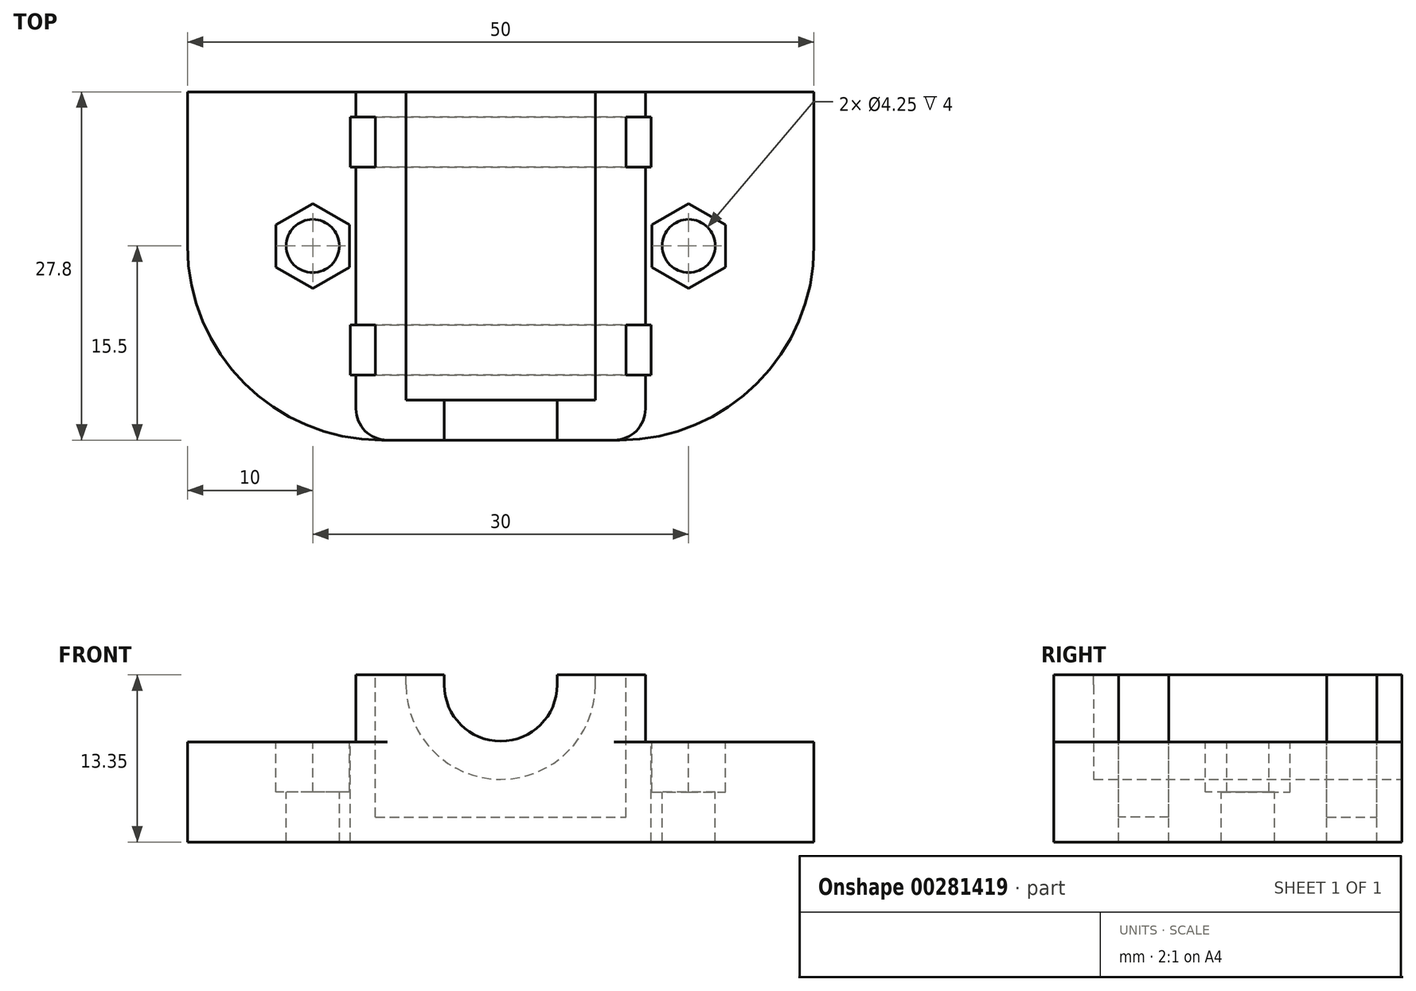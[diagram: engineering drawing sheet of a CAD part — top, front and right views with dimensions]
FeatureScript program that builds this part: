
annotation { "Feature Type Name" : "Feature", "Feature Type Description" : "" }
export const myFeature = defineFeature(function(context is Context, id is Id, definition is map)
    precondition{}
    {
        {
            var Q0;
            Q0=qCreatedBy(makeId("Front.planeOp"),FACE);
            var sketch = newSketch(context, id + "F0", { "sketchPlane" : qUnion([Q0])});
            skLineSegment(sketch, "E0.bottom", {"start": v(25, -4) * mm, "end": v(-25, -4) * mm});
            skLineSegment(sketch, "E0.top", {"start": v(25, 4) * mm, "end": v(11.55, 4) * mm});
            skLineSegment(sketch, "E0.left", {"start": v(25, -4) * mm, "end": v(25, 4) * mm});
            skLineSegment(sketch, "E0.right", {"start": v(-25, -4) * mm, "end": v(-25, 4) * mm});
            skPoint(sketch, "E0.middle", {"position": v(0, 0) * mm});
            skArc(sketch, "E1", {"start": v(7.55, 8.55) * mm, "mid": v(0, 1) * mm, "end": v(-7.55, 8.55) * mm});
            skLineSegment(sketch, "E2", {"start": v(-7.55, 9.35) * mm, "end": v(-11.55, 9.35) * mm});
            skLineSegment(sketch, "E3", {"start": v(-11.55, 9.35) * mm, "end": v(-11.55, 4) * mm});
            skLineSegment(sketch, "E4", {"start": v(-7.55, 8.55) * mm, "end": v(-7.55, 9.35) * mm});
            skLineSegment(sketch, "E5.MirrorCS", {"start": v(7.55, 8.55) * mm, "end": v(7.55, 9.35) * mm});
            skLineSegment(sketch, "E6.MirrorCS", {"start": v(7.55, 9.35) * mm, "end": v(11.55, 9.35) * mm});
            skLineSegment(sketch, "E7.MirrorCS", {"start": v(11.55, 9.35) * mm, "end": v(11.55, 4) * mm});
            skLineSegment(sketch, "E8.trimOffspring", {"start": v(-11.55, 4) * mm, "end": v(-25, 4) * mm});
            skSolve(sketch);
        }
        {
            var Q0;
            Q0=qSketchRegion(id+"F0",true);
            extrude(context, id + "F1", {"entities" : qUnion([Q0]), "endBound" : BoundingType.SYMMETRIC, "depth" : 24.6 * mm});
        }
        {
            var Q0;
            Q0=makeQuery(id+"F1.opExtrude","CAP_FACE",FACE,{"disambiguationData":[OSD([sQuery(id+"F0.wireOp",EDGE,"E0.bottom"),sQuery(id+"F0.wireOp",EDGE,"E0.top"),sQuery(id+"F0.wireOp",EDGE,"E0.left"),sQuery(id+"F0.wireOp",EDGE,"E0.right"),sQuery(id+"F0.wireOp",EDGE,"E1"),sQuery(id+"F0.wireOp",EDGE,"E2"),sQuery(id+"F0.wireOp",EDGE,"E3"),sQuery(id+"F0.wireOp",EDGE,"E4"),sQuery(id+"F0.wireOp",EDGE,"E5.MirrorCS"),sQuery(id+"F0.wireOp",EDGE,"E6.MirrorCS"),sQuery(id+"F0.wireOp",EDGE,"E7.MirrorCS"),sQuery(id+"F0.wireOp",EDGE,"E8.trimOffspring")])],"isStart":false});
            var sketch = newSketch(context, id + "F2", { "sketchPlane" : qUnion([Q0])});
            skArc(sketch, "E9", {"start": v(4.5, 8.55) * mm, "mid": v(0, 4.05) * mm, "end": v(-4.5, 8.55) * mm});
            skLineSegment(sketch, "E10", {"start": v(4.5, 8.55) * mm, "end": v(4.5, 9.35) * mm});
            skLineSegment(sketch, "E11", {"start": v(4.5, 9.35) * mm, "end": v(11.55, 9.35) * mm});
            skLineSegment(sketch, "E12", {"start": v(11.55, 9.35) * mm, "end": v(11.55, 4) * mm});
            skLineSegment(sketch, "E13", {"start": v(11.55, 4) * mm, "end": v(25, 4) * mm});
            skLineSegment(sketch, "E14", {"start": v(25, 4) * mm, "end": v(25, -4) * mm});
            skLineSegment(sketch, "E15", {"start": v(25, -4) * mm, "end": v(-25, -4) * mm});
            skLineSegment(sketch, "E16", {"start": v(-25, -4) * mm, "end": v(-25, 4) * mm});
            skLineSegment(sketch, "E17", {"start": v(-25, 4) * mm, "end": v(-11.55, 4) * mm});
            skLineSegment(sketch, "E18", {"start": v(-11.55, 4) * mm, "end": v(-11.55, 9.35) * mm});
            skLineSegment(sketch, "E19", {"start": v(-11.55, 9.35) * mm, "end": v(-4.5, 9.35) * mm});
            skLineSegment(sketch, "E20", {"start": v(-4.5, 9.35) * mm, "end": v(-4.5, 8.55) * mm});
            skSolve(sketch);
        }
        {
            var Q0;
            Q0=qSketchRegion(id+"F2",true);
            extrude(context, id + "F3", {"entities" : qUnion([Q0]), "operationType" : NewBodyOperationType.ADD, "depth" : 3.2 * mm});
        }
        {
            var Q0;
            {var subQ0=sQuery(id+"F2.wireOp",EDGE,"E17");Q0=makeQuery(id+"FOkd2pxTrmwczwa_1.1.F3.boolean.opBoolean","MERGE",FACE,{"derivedFrom":[makeQuery(id+"F3.boolean.opBoolean","MERGE",FACE,{"derivedFrom":[makeQuery(id+"F1.opExtrude","SWEPT_FACE",FACE,{"disambiguationData":[OSD([sQuery(id+"F0.wireOp",EDGE,"E8.trimOffspring")])]}),makeQuery(id+"F3.opExtrude","SWEPT_FACE",FACE,{"disambiguationData":[OSD([subQ0])]})]}),makeQuery(id+"FOkd2pxTrmwczwa_1.1.F3.opExtrude","SWEPT_FACE",FACE,{"disambiguationData":[OSD([subQ0])]})]});}
            var sketch = newSketch(context, id + "F4", { "sketchPlane" : qUnion([Q0])});
            skCircle(sketch, "E21", {"center": v(-15, 0) * mm, "radius": 2.12 * mm});
            skCircle(sketch, "E22", {"center": v(15, 0) * mm, "radius": 2.12 * mm});
            skLineSegment(sketch, "E23.bottom", {"start": v(10, 10.3) * mm, "end": v(12, 10.3) * mm});
            skLineSegment(sketch, "E23.top", {"start": v(10, 6.3) * mm, "end": v(12, 6.3) * mm});
            skLineSegment(sketch, "E23.left", {"start": v(10, 10.3) * mm, "end": v(10, 6.3) * mm});
            skLineSegment(sketch, "E23.right", {"start": v(12, 10.3) * mm, "end": v(12, 6.3) * mm});
            skLineSegment(sketch, "E24.MirrorCS", {"start": v(10, -10.3) * mm, "end": v(10, -6.3) * mm});
            skLineSegment(sketch, "E25.MirrorCS", {"start": v(12, -10.3) * mm, "end": v(12, -6.3) * mm});
            skLineSegment(sketch, "E26.MirrorCS", {"start": v(10, -10.3) * mm, "end": v(12, -10.3) * mm});
            skLineSegment(sketch, "E27.MirrorCS", {"start": v(10, -6.3) * mm, "end": v(12, -6.3) * mm});
            skLineSegment(sketch, "E28.MirrorCS", {"start": v(-10, -6.3) * mm, "end": v(-12, -6.3) * mm});
            skLineSegment(sketch, "E29.MirrorCS", {"start": v(-10, 6.3) * mm, "end": v(-12, 6.3) * mm});
            skLineSegment(sketch, "E30.MirrorCS", {"start": v(-10, -10.3) * mm, "end": v(-12, -10.3) * mm});
            skLineSegment(sketch, "E31.MirrorCS", {"start": v(-10, 10.3) * mm, "end": v(-12, 10.3) * mm});
            skLineSegment(sketch, "E32.MirrorCS", {"start": v(-12, 10.3) * mm, "end": v(-12, 6.3) * mm});
            skLineSegment(sketch, "E33.MirrorCS", {"start": v(-10, -10.3) * mm, "end": v(-10, -6.3) * mm});
            skLineSegment(sketch, "E34.MirrorCS", {"start": v(-12, -10.3) * mm, "end": v(-12, -6.3) * mm});
            skLineSegment(sketch, "E35.MirrorCS", {"start": v(-10, 10.3) * mm, "end": v(-10, 6.3) * mm});
            skSolve(sketch);
        }
        {
            var Q0;
            Q0=qSketchRegion(id+"F4",true);
            extrude(context, id + "F5", {"entities" : qUnion([Q0]), "operationType" : NewBodyOperationType.REMOVE, "endBound" : BoundingType.THROUGH_ALL, "oppositeDirection" : true, "depth" : 25 * mm});
        }
        {
            var Q0;
            {var subQ0=sQuery(id+"F2.wireOp",EDGE,"E15");Q0=makeQuery(id+"FOkd2pxTrmwczwa_1.1.F3.boolean.opBoolean","MERGE",FACE,{"derivedFrom":[makeQuery(id+"F3.boolean.opBoolean","MERGE",FACE,{"derivedFrom":[makeQuery(id+"F1.opExtrude","SWEPT_FACE",FACE,{"disambiguationData":[OSD([sQuery(id+"F0.wireOp",EDGE,"E0.bottom")])]}),makeQuery(id+"F3.opExtrude","SWEPT_FACE",FACE,{"disambiguationData":[OSD([subQ0])]})]}),makeQuery(id+"FOkd2pxTrmwczwa_1.1.F3.opExtrude","SWEPT_FACE",FACE,{"disambiguationData":[OSD([subQ0])]})]});}
            var sketch = newSketch(context, id + "F6", { "sketchPlane" : qUnion([Q0])});
            skLineSegment(sketch, "E36.bottom", {"start": v(-10, 6.3) * mm, "end": v(10, 6.3) * mm});
            skLineSegment(sketch, "E36.top", {"start": v(-10, 10.3) * mm, "end": v(10, 10.3) * mm});
            skLineSegment(sketch, "E36.left", {"start": v(-10, 6.3) * mm, "end": v(-10, 10.3) * mm});
            skLineSegment(sketch, "E36.right", {"start": v(10, 6.3) * mm, "end": v(10, 10.3) * mm});
            skLineSegment(sketch, "E37.bottom", {"start": v(-10, -6.3) * mm, "end": v(10, -6.3) * mm});
            skLineSegment(sketch, "E37.top", {"start": v(-10, -10.3) * mm, "end": v(10, -10.3) * mm});
            skLineSegment(sketch, "E37.left", {"start": v(-10, -6.3) * mm, "end": v(-10, -10.3) * mm});
            skLineSegment(sketch, "E37.right", {"start": v(10, -6.3) * mm, "end": v(10, -10.3) * mm});
            skSolve(sketch);
        }
        {
            var Q0;
            Q0=qSketchRegion(id+"F6",true);
            extrude(context, id + "F7", {"entities" : qUnion([Q0]), "operationType" : NewBodyOperationType.REMOVE, "oppositeDirection" : true, "depth" : 2 * mm});
        }
        {
            var Q0;
            Q0=makeQuery(id+"FOkd2pxTrmwczwa_1.1.F3.opExtrude","CAP_EDGE",EDGE,{"disambiguationData":[OSD([sQuery(id+"F2.wireOp",EDGE,"E16")])],"isStart":false});
            var Q1;
            Q1=makeQuery(id+"F3.opExtrude","CAP_EDGE",EDGE,{"disambiguationData":[OSD([sQuery(id+"F2.wireOp",EDGE,"E16")])],"isStart":false});
            var Q2;
            Q2=makeQuery(id+"FOkd2pxTrmwczwa_1.1.F3.opExtrude","CAP_EDGE",EDGE,{"disambiguationData":[OSD([sQuery(id+"F2.wireOp",EDGE,"E14")])],"isStart":false});
            var Q3;
            Q3=makeQuery(id+"F3.opExtrude","CAP_EDGE",EDGE,{"disambiguationData":[OSD([sQuery(id+"F2.wireOp",EDGE,"E14")])],"isStart":false});
            fillet(context, id + "F8", {"entities" : qUnion([Q0, Q1, Q2, Q3]), "radius" : 15.5 * mm, "tangentPropagation" : true, "allowEdgeOverflow" : false});
        }
        {
            var Q0;
            {var subQ0=sQuery(id+"F2.wireOp",EDGE,"E13");Q0=makeQuery(id+"FOkd2pxTrmwczwa_1.1.F3.boolean.opBoolean","MERGE",FACE,{"derivedFrom":[makeQuery(id+"F3.boolean.opBoolean","MERGE",FACE,{"derivedFrom":[makeQuery(id+"F1.opExtrude","SWEPT_FACE",FACE,{"disambiguationData":[OSD([sQuery(id+"F0.wireOp",EDGE,"E0.top")])]}),makeQuery(id+"F3.opExtrude","SWEPT_FACE",FACE,{"disambiguationData":[OSD([subQ0])]})]}),makeQuery(id+"FOkd2pxTrmwczwa_1.1.F3.opExtrude","SWEPT_FACE",FACE,{"disambiguationData":[OSD([subQ0])]})]});}
            var sketch = newSketch(context, id + "F9", { "sketchPlane" : qUnion([Q0])});
            skCircle(sketch, "E38.cCircle", {"center": v(15, 0) * mm, "radius": 2.93 * mm, "construction": true});
            skLineSegment(sketch, "E38.0", {"start": v(17.93, 1.69) * mm, "end": v(17.93, -1.69) * mm});
            skLineSegment(sketch, "E38.1", {"start": v(17.93, -1.69) * mm, "end": v(15, -3.38) * mm});
            skLineSegment(sketch, "E38.2", {"start": v(15, -3.38) * mm, "end": v(12.08, -1.69) * mm});
            skLineSegment(sketch, "E38.3", {"start": v(12.08, -1.69) * mm, "end": v(12.08, 1.69) * mm});
            skLineSegment(sketch, "E38.4", {"start": v(12.08, 1.69) * mm, "end": v(15, 3.38) * mm});
            skLineSegment(sketch, "E38.5", {"start": v(15, 3.38) * mm, "end": v(17.93, 1.69) * mm});
            skPoint(sketch, "E38.0.midPoint", {"position": v(17.93, 0) * mm});
            skLineSegment(sketch, "E39.MirrorCS", {"start": v(-12.08, -1.69) * mm, "end": v(-12.08, 1.69) * mm});
            skLineSegment(sketch, "E40.MirrorCS", {"start": v(-15, -3.38) * mm, "end": v(-12.08, -1.69) * mm});
            skLineSegment(sketch, "E41.MirrorCS", {"start": v(-17.93, 1.69) * mm, "end": v(-17.93, -1.69) * mm});
            skLineSegment(sketch, "E42.MirrorCS", {"start": v(-15, 3.38) * mm, "end": v(-17.93, 1.69) * mm});
            skLineSegment(sketch, "E43.MirrorCS", {"start": v(-12.08, 1.69) * mm, "end": v(-15, 3.38) * mm});
            skLineSegment(sketch, "E44.MirrorCS", {"start": v(-17.93, -1.69) * mm, "end": v(-15, -3.38) * mm});
            skCircle(sketch, "E45.MirrorC", {"center": v(-15, 0) * mm, "radius": 2.93 * mm, "construction": true});
            skPoint(sketch, "E46.MirrorP", {"position": v(-17.93, 0) * mm});
            skSolve(sketch);
        }
        {
            var Q0;
            Q0=qSketchRegion(id+"F9",true);
            extrude(context, id + "F10", {"entities" : qUnion([Q0]), "operationType" : NewBodyOperationType.REMOVE, "oppositeDirection" : true, "depth" : 4 * mm});
        }
        {
            var Q0;
            {var subQ0=sQuery(id+"F2.wireOp",EDGE,"E18");Q0=makeQuery(id+"F8.opFillet","BLEND_EDGE",EDGE,{"blendedFrom":[makeQuery(id+"FOkd2pxTrmwczwa_1.1.F3.opExtrude","CAP_EDGE",EDGE,{"disambiguationData":[OSD([sQuery(id+"F2.wireOp",EDGE,"E16")])],"isStart":false}),makeQuery(id+"FOkd2pxTrmwczwa_1.1.F3.boolean.opBoolean","MERGE",FACE,{"derivedFrom":[makeQuery(id+"F3.boolean.opBoolean","MERGE",FACE,{"derivedFrom":[makeQuery(id+"F1.opExtrude","SWEPT_FACE",FACE,{"disambiguationData":[OSD([sQuery(id+"F0.wireOp",EDGE,"E3")])]}),makeQuery(id+"F3.opExtrude","SWEPT_FACE",FACE,{"disambiguationData":[OSD([subQ0])]})]}),makeQuery(id+"FOkd2pxTrmwczwa_1.1.F3.opExtrude","SWEPT_FACE",FACE,{"disambiguationData":[OSD([subQ0])]})]})],"blendedInto":[makeQuery(id+"FOkd2pxTrmwczwa_1.1.F3.boolean.opBoolean","MERGE",FACE,{"derivedFrom":[makeQuery(id+"F3.boolean.opBoolean","MERGE",FACE,{"derivedFrom":[makeQuery(id+"F1.opExtrude","SWEPT_FACE",FACE,{"disambiguationData":[OSD([sQuery(id+"F0.wireOp",EDGE,"E3")])]}),makeQuery(id+"F3.opExtrude","SWEPT_FACE",FACE,{"disambiguationData":[OSD([subQ0])]})]}),makeQuery(id+"FOkd2pxTrmwczwa_1.1.F3.opExtrude","SWEPT_FACE",FACE,{"disambiguationData":[OSD([subQ0])]})]})]});}
            var Q1;
            {var subQ0=sQuery(id+"F2.wireOp",EDGE,"E12");Q1=makeQuery(id+"F8.opFillet","BLEND_EDGE",EDGE,{"blendedFrom":[makeQuery(id+"FOkd2pxTrmwczwa_1.1.F3.opExtrude","CAP_EDGE",EDGE,{"disambiguationData":[OSD([sQuery(id+"F2.wireOp",EDGE,"E14")])],"isStart":false}),makeQuery(id+"FOkd2pxTrmwczwa_1.1.F3.boolean.opBoolean","MERGE",FACE,{"derivedFrom":[makeQuery(id+"F3.boolean.opBoolean","MERGE",FACE,{"derivedFrom":[makeQuery(id+"F1.opExtrude","SWEPT_FACE",FACE,{"disambiguationData":[OSD([sQuery(id+"F0.wireOp",EDGE,"E7.MirrorCS")])]}),makeQuery(id+"F3.opExtrude","SWEPT_FACE",FACE,{"disambiguationData":[OSD([subQ0])]})]}),makeQuery(id+"FOkd2pxTrmwczwa_1.1.F3.opExtrude","SWEPT_FACE",FACE,{"disambiguationData":[OSD([subQ0])]})]})],"blendedInto":[makeQuery(id+"FOkd2pxTrmwczwa_1.1.F3.boolean.opBoolean","MERGE",FACE,{"derivedFrom":[makeQuery(id+"F3.boolean.opBoolean","MERGE",FACE,{"derivedFrom":[makeQuery(id+"F1.opExtrude","SWEPT_FACE",FACE,{"disambiguationData":[OSD([sQuery(id+"F0.wireOp",EDGE,"E7.MirrorCS")])]}),makeQuery(id+"F3.opExtrude","SWEPT_FACE",FACE,{"disambiguationData":[OSD([subQ0])]})]}),makeQuery(id+"FOkd2pxTrmwczwa_1.1.F3.opExtrude","SWEPT_FACE",FACE,{"disambiguationData":[OSD([subQ0])]})]})]});}
            var Q2;
            {var subQ0=sQuery(id+"F2.wireOp",EDGE,"E18");Q2=makeQuery(id+"F8.opFillet","BLEND_EDGE",EDGE,{"blendedFrom":[makeQuery(id+"F3.opExtrude","CAP_EDGE",EDGE,{"disambiguationData":[OSD([sQuery(id+"F2.wireOp",EDGE,"E16")])],"isStart":false}),makeQuery(id+"FOkd2pxTrmwczwa_1.1.F3.boolean.opBoolean","MERGE",FACE,{"derivedFrom":[makeQuery(id+"F3.boolean.opBoolean","MERGE",FACE,{"derivedFrom":[makeQuery(id+"F1.opExtrude","SWEPT_FACE",FACE,{"disambiguationData":[OSD([sQuery(id+"F0.wireOp",EDGE,"E3")])]}),makeQuery(id+"F3.opExtrude","SWEPT_FACE",FACE,{"disambiguationData":[OSD([subQ0])]})]}),makeQuery(id+"FOkd2pxTrmwczwa_1.1.F3.opExtrude","SWEPT_FACE",FACE,{"disambiguationData":[OSD([subQ0])]})]})],"blendedInto":[makeQuery(id+"FOkd2pxTrmwczwa_1.1.F3.boolean.opBoolean","MERGE",FACE,{"derivedFrom":[makeQuery(id+"F3.boolean.opBoolean","MERGE",FACE,{"derivedFrom":[makeQuery(id+"F1.opExtrude","SWEPT_FACE",FACE,{"disambiguationData":[OSD([sQuery(id+"F0.wireOp",EDGE,"E3")])]}),makeQuery(id+"F3.opExtrude","SWEPT_FACE",FACE,{"disambiguationData":[OSD([subQ0])]})]}),makeQuery(id+"FOkd2pxTrmwczwa_1.1.F3.opExtrude","SWEPT_FACE",FACE,{"disambiguationData":[OSD([subQ0])]})]})]});}
            var Q3;
            {var subQ0=sQuery(id+"F2.wireOp",EDGE,"E12");Q3=makeQuery(id+"F8.opFillet","BLEND_EDGE",EDGE,{"blendedFrom":[makeQuery(id+"F3.opExtrude","CAP_EDGE",EDGE,{"disambiguationData":[OSD([sQuery(id+"F2.wireOp",EDGE,"E14")])],"isStart":false}),makeQuery(id+"FOkd2pxTrmwczwa_1.1.F3.boolean.opBoolean","MERGE",FACE,{"derivedFrom":[makeQuery(id+"F3.boolean.opBoolean","MERGE",FACE,{"derivedFrom":[makeQuery(id+"F1.opExtrude","SWEPT_FACE",FACE,{"disambiguationData":[OSD([sQuery(id+"F0.wireOp",EDGE,"E7.MirrorCS")])]}),makeQuery(id+"F3.opExtrude","SWEPT_FACE",FACE,{"disambiguationData":[OSD([subQ0])]})]}),makeQuery(id+"FOkd2pxTrmwczwa_1.1.F3.opExtrude","SWEPT_FACE",FACE,{"disambiguationData":[OSD([subQ0])]})]})],"blendedInto":[makeQuery(id+"FOkd2pxTrmwczwa_1.1.F3.boolean.opBoolean","MERGE",FACE,{"derivedFrom":[makeQuery(id+"F3.boolean.opBoolean","MERGE",FACE,{"derivedFrom":[makeQuery(id+"F1.opExtrude","SWEPT_FACE",FACE,{"disambiguationData":[OSD([sQuery(id+"F0.wireOp",EDGE,"E7.MirrorCS")])]}),makeQuery(id+"F3.opExtrude","SWEPT_FACE",FACE,{"disambiguationData":[OSD([subQ0])]})]}),makeQuery(id+"FOkd2pxTrmwczwa_1.1.F3.opExtrude","SWEPT_FACE",FACE,{"disambiguationData":[OSD([subQ0])]})]})]});}
            var Q4;
            Q4=makeQuery(id+"F7.boolean.opBoolean","COPY",EDGE,{"derivedFrom":makeQuery(id+"F7.opExtrude","CAP_EDGE",EDGE,{"disambiguationData":[OSD([sQuery(id+"F6.wireOp",EDGE,"E36.left")])],"isStart":false})});
            var Q5;
            Q5=makeQuery(id+"F7.boolean.opBoolean","COPY",EDGE,{"derivedFrom":makeQuery(id+"F7.opExtrude","CAP_EDGE",EDGE,{"disambiguationData":[OSD([sQuery(id+"F6.wireOp",EDGE,"E36.right")])],"isStart":false})});
            var Q6;
            Q6=makeQuery(id+"F7.boolean.opBoolean","COPY",EDGE,{"derivedFrom":makeQuery(id+"F7.opExtrude","CAP_EDGE",EDGE,{"disambiguationData":[OSD([sQuery(id+"F6.wireOp",EDGE,"E37.right")])],"isStart":false})});
            var Q7;
            Q7=makeQuery(id+"F7.boolean.opBoolean","COPY",EDGE,{"derivedFrom":makeQuery(id+"F7.opExtrude","CAP_EDGE",EDGE,{"disambiguationData":[OSD([sQuery(id+"F6.wireOp",EDGE,"E37.left")])],"isStart":false})});
            fillet(context, id + "F11", {"entities" : qUnion([Q0, Q1, Q2, Q3, Q4, Q5, Q6, Q7]), "radius" : 2.5 * mm, "tangentPropagation" : true, "allowEdgeOverflow" : false});
        }
        {
            var Q0;
            Q0=makeQuery(id+"F5.boolean.opBoolean","COPY",FACE,{"derivedFrom":makeQuery(id+"F5.opExtrude","CAP_FACE",FACE,{"disambiguationData":[OSD([sQuery(id+"F4.wireOp",EDGE,"E28.MirrorCS"),sQuery(id+"F4.wireOp",EDGE,"E30.MirrorCS"),sQuery(id+"F4.wireOp",EDGE,"E33.MirrorCS"),sQuery(id+"F4.wireOp",EDGE,"E34.MirrorCS")])],"isStart":true})});
            var sketch = newSketch(context, id + "F12", { "sketchPlane" : qUnion([Q0])});
            skLineSegment(sketch, "E47.bottom", {"start": v(-11.55, 10.3) * mm, "end": v(-10, 10.3) * mm});
            skLineSegment(sketch, "E47.top", {"start": v(-11.55, 6.3) * mm, "end": v(-10, 6.3) * mm});
            skLineSegment(sketch, "E47.left", {"start": v(-11.55, 10.3) * mm, "end": v(-11.55, 6.3) * mm});
            skLineSegment(sketch, "E47.right", {"start": v(-10, 10.3) * mm, "end": v(-10, 6.3) * mm});
            skLineSegment(sketch, "E48.MirrorCS", {"start": v(10, 10.3) * mm, "end": v(10, 6.3) * mm});
            skLineSegment(sketch, "E49.MirrorCS", {"start": v(11.55, 10.3) * mm, "end": v(11.55, 6.3) * mm});
            skLineSegment(sketch, "E50.MirrorCS", {"start": v(11.55, 6.3) * mm, "end": v(10, 6.3) * mm});
            skLineSegment(sketch, "E51.MirrorCS", {"start": v(11.55, 10.3) * mm, "end": v(10, 10.3) * mm});
            skLineSegment(sketch, "E52.MirrorCS", {"start": v(11.55, -10.3) * mm, "end": v(10, -10.3) * mm});
            skLineSegment(sketch, "E53.MirrorCS", {"start": v(-11.55, -10.3) * mm, "end": v(-10, -10.3) * mm});
            skLineSegment(sketch, "E54.MirrorCS", {"start": v(-11.55, -6.3) * mm, "end": v(-10, -6.3) * mm});
            skLineSegment(sketch, "E55.MirrorCS", {"start": v(11.55, -6.3) * mm, "end": v(10, -6.3) * mm});
            skLineSegment(sketch, "E56.MirrorCS", {"start": v(-11.55, -10.3) * mm, "end": v(-11.55, -6.3) * mm});
            skLineSegment(sketch, "E57.MirrorCS", {"start": v(-10, -10.3) * mm, "end": v(-10, -6.3) * mm});
            skLineSegment(sketch, "E58.MirrorCS", {"start": v(10, -10.3) * mm, "end": v(10, -6.3) * mm});
            skLineSegment(sketch, "E59.MirrorCS", {"start": v(11.55, -10.3) * mm, "end": v(11.55, -6.3) * mm});
            skSolve(sketch);
        }
        {
            var Q0;
            Q0=qSketchRegion(id+"F12",true);
            extrude(context, id + "F13", {"entities" : qUnion([Q0]), "operationType" : NewBodyOperationType.REMOVE, "oppositeDirection" : true, "depth" : 25 * mm});
        }
    });
